# Revit family: Control_Panels-Lutron-DIN_Rail_Retrofit_Subplate (1)
name_source: partatom
category: Electrical Equipment
units: mm (PartAtom-declared; Revit-internal decimal feet)

## family parameters
Cut with Voids When Loaded = No
Host = Face
OmniClass Number = 23.80.30.11.17
OmniClass Title = Distribution Boards and Control Panels
Panel Configuration = Two Columns, Circuits Across
Part Type = Panelboard
Room Calculation Point = No
Round Connector Dimension = Use Radius
Shared = No

## types (1)
- HWR-PD-8-120FT
    Assembly Code = D5010200
    Bussing = To Be Defined
    C Electrical Connector Distance = 38 "
    Cost = 0 $
    Default Elevation = 0 "
    Description = DIN Rail Retrofit Subplate for LiteTouch Enclosures
    Electrical Potential = 120 V
    Feed Through Control Circuit Voltage = 120 V
    Finish = Steel - Lutron - Black
    Frequency = 60 Hz
    Ground Bus = No
    Instruction Sheet Link = https://assets.lutron.com
    Keynote = 16400
    Load Classification = Power
    Mains Type = To Be Defined
    Manufacturer = Lutron Electronics Co., Inc
    Manufacturer Fax Number = Consult Manufacturer Website for More Information
    Model = HWR-PD-8-120FT
    Neutral Bus = No
    Neutral Rating = 0.00%
    Number of Poles = 1
    Overall Depth = 2 "
    Overall Height = 39 "
    Overall Width = 22 "
    Performance URL = http://www.lutron.com
    Phase = 1
    Power Factor = 1
    Product Documentation Link = https://assets.lutron.com
    Product Name = DIN Rail Retrofit Subplate
    Product Page URL = https://residential.lutron.com
    Series = HomeWorks
    URL = http://www.lutron.com
    Version = 2020 - v1.0a
    Video Link = https://www.youtube.com
    Voltage = 120.00 V
    Warranty URL = www.lutron.com/TechnicalDocumentLibrary/Warranty.pdf
    Wattage = To Be Defined

## geometry (parser evidence)
native form markers: Sweep x7
no freeform markers — native parametric forms only
